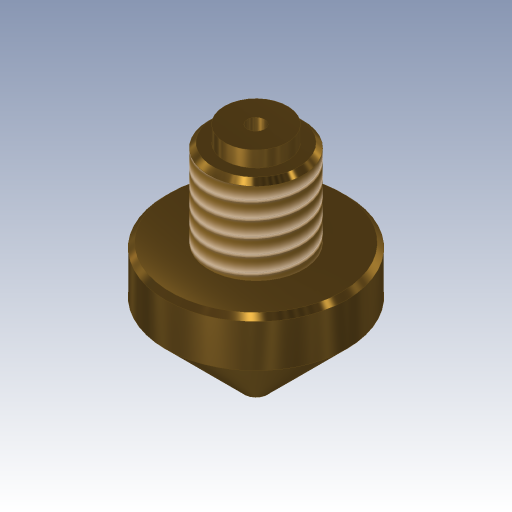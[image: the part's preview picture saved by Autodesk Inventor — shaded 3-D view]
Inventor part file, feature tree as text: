
AUTODESK INVENTOR PART (.ipt)
format: ipt  version: 2023.3 (Build 273359000, 359)  size: 209,920 bytes
history: native  units: in
note: dims shown in document units (in); Inventor stores cm internally (conversion verified against a paired STEP export)
features: revolve x1, thread x1, chamfer x1, sketch x1
ambient origin geometry x8: Origin, YZ Plane, XZ Plane, XY Plane, X Axis, Y Axis, Z Axis, Center Point
bodies: Body1 (feature_tree)
feature tree (4):
  revolve  "Umdrehung1"
  thread  "Gewinde1"  [1 undecoded]
  chamfer  "Fase1"  Distance=0.2362in
  sketch  "Skizze3"  dims[d9=0.4528in d11=0.2362in d12=0.1575in d13=0.0394in d15=0.0433in d16=360.0deg d17=0.5906in d18=0.0in d19=0.0118in d20=0.0787in d21=45.0deg d37=45.0deg d38=0.1181in d39=0.2559in]
note: 1 required parameter value undecoded (feature->parameter linkage not recoverable at this tier; creation-order binding heuristic only, values carry confidence <= 0.55)
